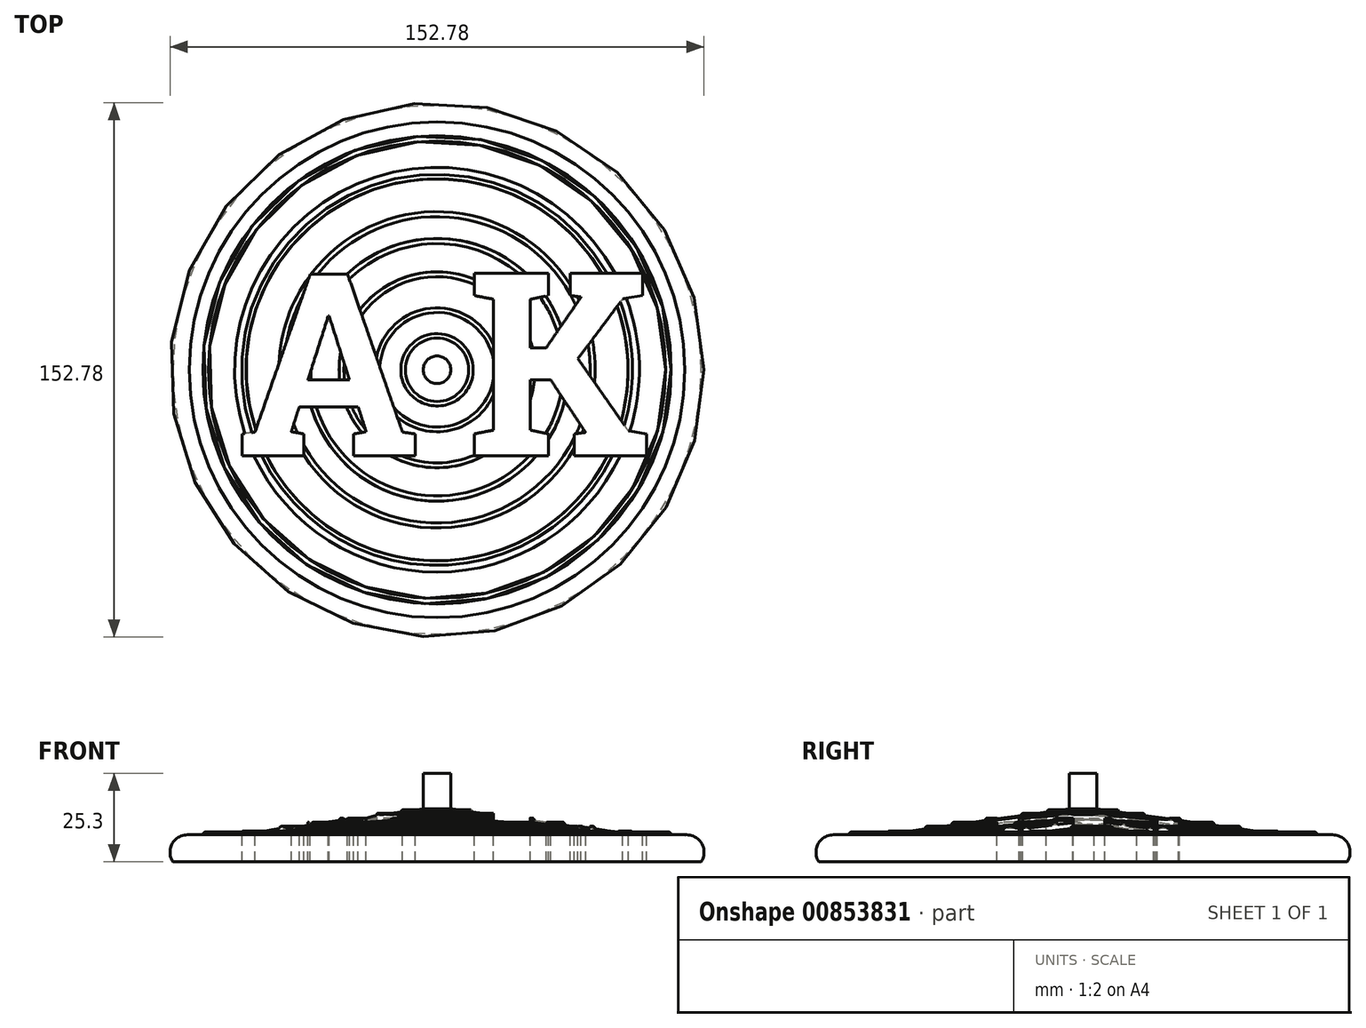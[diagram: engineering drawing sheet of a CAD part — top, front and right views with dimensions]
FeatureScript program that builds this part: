
annotation { "Feature Type Name" : "Feature", "Feature Type Description" : "" }
export const myFeature = defineFeature(function(context is Context, id is Id, definition is map)
    precondition{}
    {
        {
            var Q0;
            Q0=qCreatedBy(makeId("Front.planeOp"),FACE);
            var sketch = newSketch(context, id + "F0", { "sketchPlane" : qUnion([Q0])});
            skArc(sketch, "E0", {"start": v(-70.87, 7.7) * mm, "mid": v(-75.65, 5.33) * mm, "end": v(-75.58, 0) * mm});
            skLineSegment(sketch, "E1", {"start": v(-70.87, 7.7) * mm, "end": v(-67, 7.7) * mm});
            skLineSegment(sketch, "E2", {"start": v(-57.88, 7.7) * mm, "end": v(-55.86, 7.97) * mm});
            skArc(sketch, "E3", {"start": v(-65.4, 7.7) * mm, "mid": v(-66.2, 8.5) * mm, "end": v(-67, 7.7) * mm});
            skArc(sketch, "E4", {"start": v(-54.63, 8.14) * mm, "mid": v(-55.35, 8.84) * mm, "end": v(-55.86, 7.97) * mm});
            skArc(sketch, "E5", {"start": v(-43.8, 9.64) * mm, "mid": v(-44.6, 10.14) * mm, "end": v(-45.23, 9.44) * mm});
            skArc(sketch, "E6", {"start": v(-36.08, 10.7) * mm, "mid": v(-36.92, 11.32) * mm, "end": v(-37.56, 10.5) * mm});
            skArc(sketch, "E7", {"start": v(-26.61, 12) * mm, "mid": v(-27.39, 12.52) * mm, "end": v(-28, 11.82) * mm});
            skArc(sketch, "E8", {"start": v(-16.4, 13.42) * mm, "mid": v(-17.12, 13.87) * mm, "end": v(-17.7, 13.24) * mm});
            skArc(sketch, "E9", {"start": v(-9.07, 14.43) * mm, "mid": v(-9.78, 14.84) * mm, "end": v(-10.35, 14.25) * mm});
            skLineSegment(sketch, "E10", {"start": v(-3.94, 16.97) * mm, "end": v(-3.94, 15.38) * mm});
            skLineSegment(sketch, "E11", {"start": v(-3.94, 15.38) * mm, "end": v(-3.94, 15.14) * mm});
            skLineSegment(sketch, "E12", {"start": v(-3.94, 16.97) * mm, "end": v(-3.94, 25.3) * mm});
            skLineSegment(sketch, "E13", {"start": v(-3.94, 25.3) * mm, "end": v(0, 25.3) * mm});
            skPoint(sketch, "E14.end.orphan", {"position": v(0, 16.97) * mm});
            skPoint(sketch, "E14.start.orphan", {"position": v(-0.66, 16.97) * mm});
            skLineSegment(sketch, "E15", {"start": v(0, 25.3) * mm, "end": v(0, 0) * mm});
            skLineSegment(sketch, "E16.trimOffspring", {"start": v(-65.4, 7.7) * mm, "end": v(-57.88, 7.7) * mm});
            skLineSegment(sketch, "E17.trimOffspring", {"start": v(-54.63, 8.14) * mm, "end": v(-45.23, 9.44) * mm});
            skLineSegment(sketch, "E18.trimOffspring", {"start": v(-43.8, 9.64) * mm, "end": v(-37.56, 10.5) * mm});
            skLineSegment(sketch, "E19.trimOffspring", {"start": v(-36.08, 10.7) * mm, "end": v(-28, 11.82) * mm});
            skLineSegment(sketch, "E20.trimOffspring", {"start": v(-26.61, 12) * mm, "end": v(-17.7, 13.24) * mm});
            skLineSegment(sketch, "E21.trimOffspring", {"start": v(-16.4, 13.42) * mm, "end": v(-10.35, 14.25) * mm});
            skLineSegment(sketch, "E22.trimOffspring", {"start": v(-9.07, 14.43) * mm, "end": v(-3.94, 15.14) * mm});
            skPoint(sketch, "E23.orphan", {"position": v(0, 15.68) * mm});
            skLineSegment(sketch, "E24", {"start": v(-75.58, 0) * mm, "end": v(0, 0) * mm});
            skSolve(sketch);
        }
        {
            var Q0;
            Q0 = qSketchRegion(id + "F0", true);
            var Q1;
            Q1=sQuery(id+"F0.wireOp",EDGE,"E15");
            revolve(context, id + "F1", {"surfaceOperationType" : NewSurfaceOperationType.NEW, "entities" : qUnion([Q0]), "axis" : qUnion([Q1]), "revolveType" : RevolveType.FULL});
        }
        {
            var Q0;
            Q0=qCreatedBy(makeId("Top.planeOp"),FACE);
            var sketch = newSketch(context, id + "F2", { "sketchPlane" : qUnion([Q0])});
            skText(sketch, "E25", { "text": "A", "fontName": "RobotoSlab-Bold.ttf"});
            skText(sketch, "E26", { "text": "K", "fontName": "RobotoSlab-Bold.ttf"});
            const initialGuessF2  = {"E25": [-0.05725, -0.02459, 1, 0, 0.05262], "E26": [0.00862, -0.02459, 1, 0, 0.0528]};
            skSetInitialGuess(sketch, initialGuessF2);
            skSolve(sketch);
        }
        {
            var Q0;
            Q0 = qSketchRegion(id + "F2", true);
            extrude(context, id + "F3", {"entities" : qUnion([Q0]), "operationType" : NewBodyOperationType.REMOVE, "endBound" : BoundingType.SYMMETRIC, "oppositeDirection" : true, "depth" : 127 * mm, "offsetDistance" : 25.4 * mm});
        }
    });
